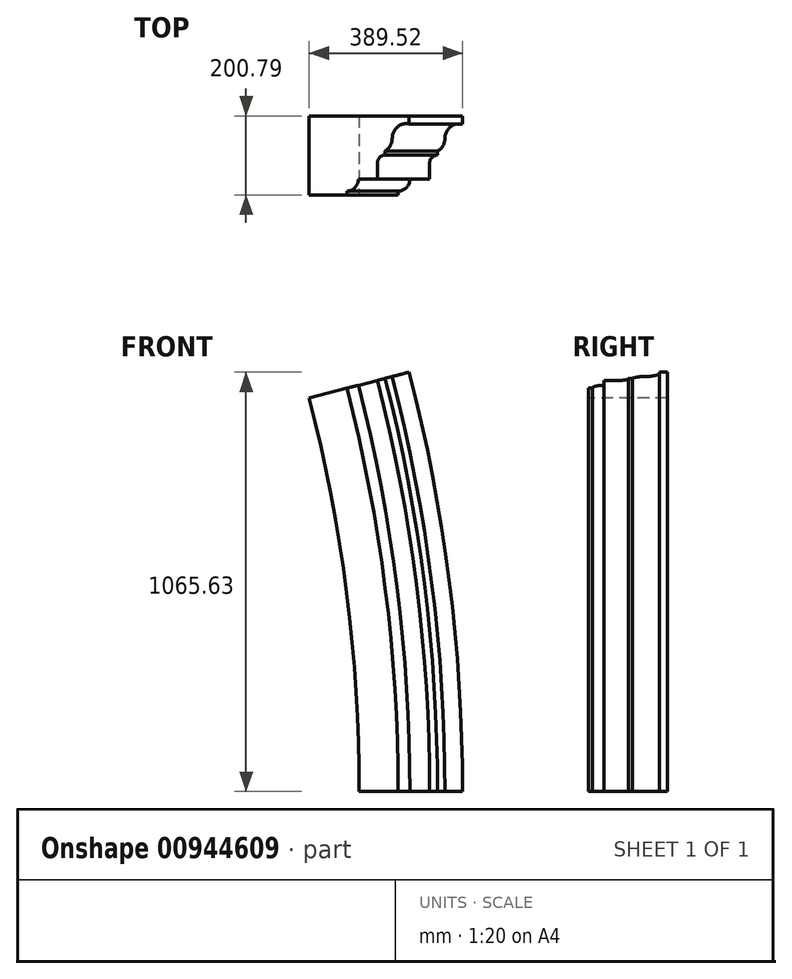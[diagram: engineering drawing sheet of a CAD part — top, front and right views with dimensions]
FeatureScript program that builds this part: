
annotation { "Feature Type Name" : "Feature", "Feature Type Description" : "" }
export const myFeature = defineFeature(function(context is Context, id is Id, definition is map)
    precondition{}
    {
        {
            var Q0;
            Q0=qCreatedBy(makeId("Top.planeOp"),FACE);
            var sketch = newSketch(context, id + "F0", { "sketchPlane" : qUnion([Q0])});
            skLineSegment(sketch, "E0", {"start": v(-101.25, 154.39) * mm, "end": v(161.25, 154.39) * mm});
            skLineSegment(sketch, "E1", {"start": v(161.25, 154.39) * mm, "end": v(161.25, 134.39) * mm});
            skLineSegment(sketch, "E2", {"start": v(-101.25, 154.39) * mm, "end": v(-101.25, -46.4) * mm});
            skLineSegment(sketch, "E3", {"start": v(77.72, 55) * mm, "end": v(97.72, 55) * mm, "construction": true});
            skLineSegment(sketch, "E4", {"start": v(97.72, 55) * mm, "end": v(97.72, 65) * mm});
            skArc(sketch, "E5", {"start": v(97.72, 65) * mm, "mid": v(111.56, 78.74) * mm, "end": v(116.63, 97.57) * mm});
            skArc(sketch, "E6", {"start": v(161.25, 134.39) * mm, "mid": v(130.26, 126.5) * mm, "end": v(116.63, 97.57) * mm});
            skLineSegment(sketch, "E7", {"start": v(77.72, 35) * mm, "end": v(77.72, -6.4) * mm});
            skLineSegment(sketch, "E8", {"start": v(97.72, 55) * mm, "end": v(97.72, 35) * mm, "construction": true});
            skArc(sketch, "E9", {"start": v(97.72, 55) * mm, "mid": v(83.57, 49.14) * mm, "end": v(77.72, 35) * mm});
            skLineSegment(sketch, "E10", {"start": v(77.72, -6.4) * mm, "end": v(27.72, -6.4) * mm});
            skLineSegment(sketch, "E11", {"start": v(27.72, -6.4) * mm, "end": v(-2.28, -6.4) * mm, "construction": true});
            skArc(sketch, "E12", {"start": v(27.72, -6.4) * mm, "mid": v(18.93, -27.61) * mm, "end": v(-2.28, -36.4) * mm});
            skLineSegment(sketch, "E13", {"start": v(-2.28, -36.4) * mm, "end": v(-2.28, -46.4) * mm});
            skLineSegment(sketch, "E14", {"start": v(-2.28, -46.4) * mm, "end": v(-101.25, -46.4) * mm});
            skSolve(sketch);
        }
        {
            var Q0;
            Q0=qCreatedBy(makeId("Front.planeOp"),FACE);
            var Q1;
            Q1=sQuery(id+"F0.wireOp",VERTEX,"E2.end");
            cPlane(context, id + "F1", {"entities" : qUnion([Q0, Q1]), "cplaneType" : CPlaneType.PLANE_POINT, "offset" : 25 * mm, "width" : 150 * mm, "height" : 150 * mm});
        }
        {
            var Q0;
            Q0=qCreatedBy(id+"F1.planeOp",FACE);
            var sketch = newSketch(context, id + "F2", { "sketchPlane" : qUnion([Q0])});
            skPoint(sketch, "E15.0", {"position": v(-101.25, 0) * mm});
            skLineSegment(sketch, "E16", {"start": v(-101.25, 0) * mm, "end": v(-4101.25, 0) * mm, "construction": true});
            skLineSegment(sketch, "E17", {"start": v(-4101.25, 0) * mm, "end": v(-4101.25, 4000) * mm, "construction": true});
            skArc(sketch, "E18", {"start": v(-101.25, 0) * mm, "mid": v(-133.13, 504.02) * mm, "end": v(-228.27, 1000) * mm});
            skSolve(sketch);
        }
        {
            var Q0;
            Q0=makeQuery(id+"F0.imprint","IMPRINT",FACE,{"disambiguationData":[TD([[makeQuery(id+"F0.imprint","IMPRINT",EDGE,{"derivedFrom":sQuery(id+"F0.wireOp",EDGE,"E0")}),-1.0]])]});
            var Q1;
            Q1=sQuery(id+"F2.wireOp",EDGE,"E18");
            sweep(context, id + "F3", {"profiles" : qUnion([Q0]), "path" : qUnion([Q1])});
        }
    });
